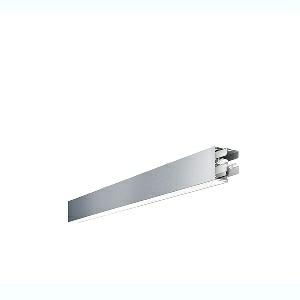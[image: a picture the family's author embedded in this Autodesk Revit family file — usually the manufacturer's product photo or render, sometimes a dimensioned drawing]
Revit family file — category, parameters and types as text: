
# Revit family: dotoo_line_-_dla_1000_830_d_mid_00807962_9d27
name_source: partatom
category: Lighting Fixtures
units: mm (PartAtom-declared; Revit-internal decimal feet)

## family parameters
Cut with Voids When Loaded = No
Host = Face
Light Source = No
Part Type = Normal
Room Calculation Point = No
Round Connector Dimension = Use Diameter
Shared = No

## types (1)
- DOTOO.line - DLA 1000/830/D MID (1 x LED, 1000 lm, 3000K)
    Apparent Load = 10 VA
    Approval mark = CE
    CIE Flux Codes = 67 91 98 100 100
    Color Rendering = 80-89
    Color Temperature = 3000K
    Control Gear = Electronic ballast
    Default Elevation = 1800 mm
    Description = DLA 1000/830/D|Surface-mounted luminaire.|light source: LED|work equipment: Adjustable electronic ballast, digital DALI|connected load: 220-240 V, 50/60 Hz|Power consumption: approx. 10 W|luminous flux: 1000 lm|luminous efficacy: 100 lm/W|light distribution: Direct|colour temperature: Warm white, ca. 3000 K|class of protection: I|technology: Continuously dimmable|mains lead: Connector|glare control: Prism aperture|special features: DALI Load 1x, TouchDIM - dimming via standard switch, Through-wired, up to 18 m on one mains connection, Flicker-free, Suitable as emergency lighting, Mechanical and electrical connection of the individual modules without tools|
    Frequency = 50 Hz
    Height = 110 mm
    Lamp = 1 x LED
    Lamp Light Flux = 1000 lm
    Lamp count = 1
    Length = 842 mm
    Luminous efficacy = 100 lm/W
    Manufacturer = Waldmann
    ModVariant = No
    Model = 00807962
    Mounting Place = Ceiling
    Mounting Type = Surface mounted
    Number of Poles = 1
    OnlyDefault = Yes
    Power Factor = 1
    Product Name = DOTOO.line - DLA 1000/830/D MID
    Product group = Ceiling mounted luminaire
    ProductGroupID = 3
    Protection Class = Protection class I
    Protection Degree = IP 40
    RLX_Detail_Level = 1
    RLX_Emergency_Light_Flux = 0 lm
    RLX_Emergency_Type = 0
    RLX_Emergency_Type_DB = No
    RlxData = <blob elided: 18085 chars, md5=307de4c2>
    Socket = socket
    Standby Power = 0 W
    System Light Flux = 1000 lm
    System Power = 10 W
    Type Comments = Product without accessories
    Type Image = 114373000-00807950.jpg
    URL = http://relux.com
    VarID = ---
    Voltage = 230 V
    Voltage Range = 220-240 V
    Weight = 0.00 kg
    Width = 60 mm  [stored 0.19685 ft]

note: [stored X ft] marks values corroborated as IEEE doubles in the binary element streams (Revit-internal decimal feet)

## geometry (parser evidence)
native form markers: Blend x4, Sweep x12
no freeform markers — native parametric forms only
